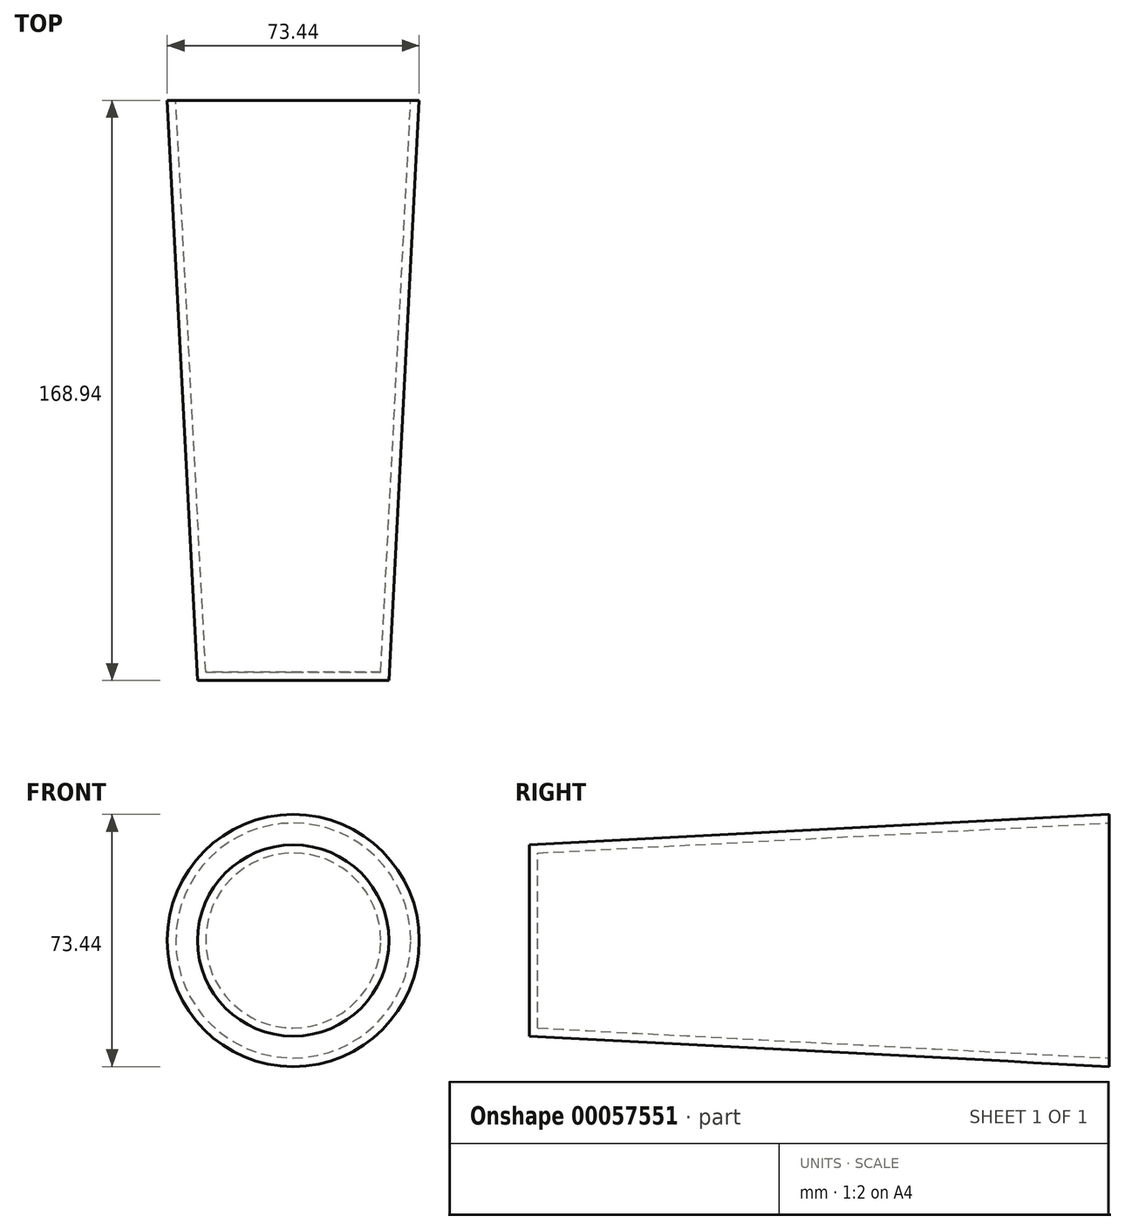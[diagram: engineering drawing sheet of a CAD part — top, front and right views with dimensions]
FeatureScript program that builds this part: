
annotation { "Feature Type Name" : "Feature", "Feature Type Description" : "" }
export const myFeature = defineFeature(function(context is Context, id is Id, definition is map)
    precondition{}
    {
        {
            var Q0;
            Q0=qCreatedBy(makeId("Front.planeOp"),FACE);
            var sketch = newSketch(context, id + "F0", { "sketchPlane" : qUnion([Q0])});
            skCircle(sketch, "E0", {"center": v(0, 0) * mm, "radius": 36.72 * mm});
            skSolve(sketch);
        }
        {
            var Q0;
            Q0=makeQuery(id+"F0.imprint","IMPRINT",FACE,{"disambiguationData":[TD([[makeQuery(id+"F0.imprint","IMPRINT",EDGE,{"derivedFrom":sQuery(id+"F0.wireOp",EDGE,"E0")}),1.0]])]});
            extrude(context, id + "F1", {"entities" : qUnion([Q0]), "depth" : 168.94 * mm, "hasDraft" : true, "draftAngle" : 3 * degree, "draftPullDirection" : true});
        }
        {
            var Q0;
            Q0=makeQuery(id+"F1.opExtrude","CAP_FACE",FACE,{"disambiguationData":[OSD([sQuery(id+"F0.wireOp",EDGE,"E0")])],"isStart":true});
            shell(context, id + "F2", {"entities" : qUnion([Q0]), "thickness" : 2.5 * mm});
        }
    });
